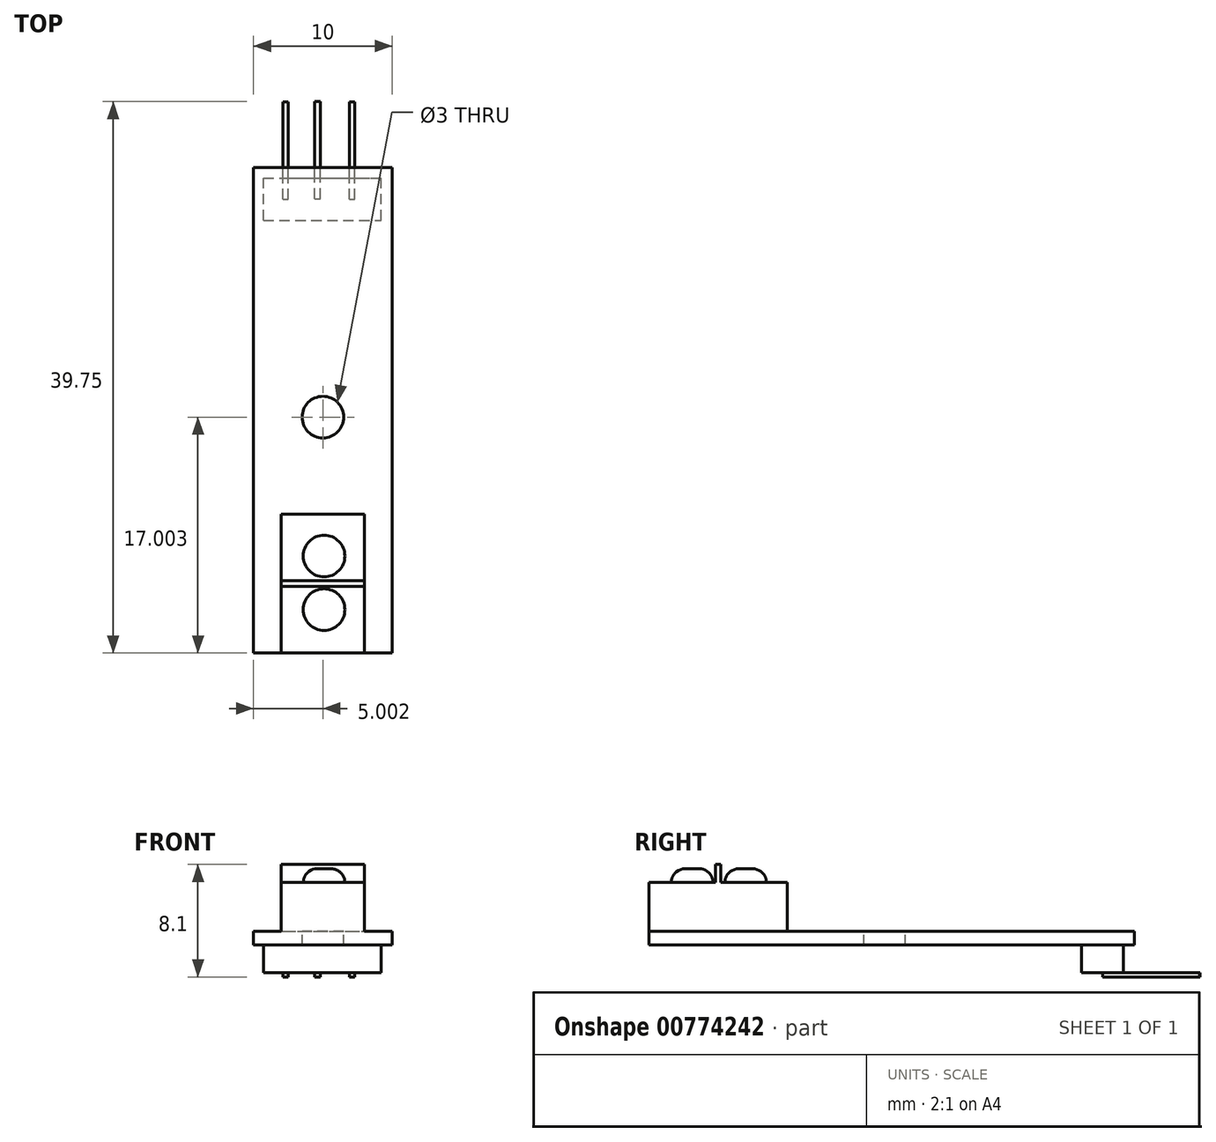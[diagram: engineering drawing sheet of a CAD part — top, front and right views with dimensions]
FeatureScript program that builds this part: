
annotation { "Feature Type Name" : "Feature", "Feature Type Description" : "" }
export const myFeature = defineFeature(function(context is Context, id is Id, definition is map)
    precondition{}
    {
        {
            var Q0;
            Q0=qCreatedBy(makeId("Top.planeOp"),FACE);
            var sketch = newSketch(context, id + "F0", { "sketchPlane" : qUnion([Q0])});
            skLineSegment(sketch, "E0.bottom", {"start": v(-16.49, 28.01) * mm, "end": v(-6.49, 28.01) * mm});
            skLineSegment(sketch, "E0.top", {"start": v(-16.49, -6.99) * mm, "end": v(-6.49, -6.99) * mm});
            skLineSegment(sketch, "E0.left", {"start": v(-16.49, 28.01) * mm, "end": v(-16.49, -6.99) * mm});
            skLineSegment(sketch, "E0.right", {"start": v(-6.49, 28.01) * mm, "end": v(-6.49, -6.99) * mm});
            skSolve(sketch);
        }
        {
            var Q0;
            Q0 = qSketchRegion(id + "F0", true);
            extrude(context, id + "F1", {"entities" : qUnion([Q0]), "depth" : 1 * mm, "offsetDistance" : 25 * mm});
        }
        {
            var Q0;
            Q0=makeQuery(id+"F1.opExtrude","CAP_FACE",FACE,{"disambiguationData":[OSD([sQuery(id+"F0.wireOp",EDGE,"E0.bottom"),sQuery(id+"F0.wireOp",EDGE,"E0.top"),sQuery(id+"F0.wireOp",EDGE,"E0.left"),sQuery(id+"F0.wireOp",EDGE,"E0.right")])],"isStart":false});
            var sketch = newSketch(context, id + "F2", { "sketchPlane" : qUnion([Q0])});
            skLineSegment(sketch, "E1.bottom", {"start": v(-14.49, -6.99) * mm, "end": v(-8.49, -6.99) * mm});
            skLineSegment(sketch, "E1.top", {"start": v(-14.49, 3.01) * mm, "end": v(-8.49, 3.01) * mm});
            skLineSegment(sketch, "E1.left", {"start": v(-14.49, -6.99) * mm, "end": v(-14.49, 3.01) * mm});
            skLineSegment(sketch, "E1.right", {"start": v(-8.49, -6.99) * mm, "end": v(-8.49, 3.01) * mm});
            skSolve(sketch);
        }
        {
            var Q0;
            Q0 = qSketchRegion(id + "F2", true);
            extrude(context, id + "F3", {"entities" : qUnion([Q0]), "operationType" : NewBodyOperationType.ADD, "depth" : 3.5 * mm, "offsetDistance" : 25 * mm});
        }
        {
            var Q0;
            Q0=makeQuery(id+"F3.opExtrude","CAP_FACE",FACE,{"disambiguationData":[OSD([sQuery(id+"F2.wireOp",EDGE,"E1.bottom"),sQuery(id+"F2.wireOp",EDGE,"E1.top"),sQuery(id+"F2.wireOp",EDGE,"E1.left"),sQuery(id+"F2.wireOp",EDGE,"E1.right")])],"isStart":false});
            var sketch = newSketch(context, id + "F4", { "sketchPlane" : qUnion([Q0])});
            skLineSegment(sketch, "E2", {"start": v(-14.49, -1.99) * mm, "end": v(-8.49, -1.99) * mm});
            skCircle(sketch, "E3", {"center": v(-11.4, -3.86) * mm, "radius": 1.5 * mm});
            skCircle(sketch, "E4", {"center": v(-11.4, 0) * mm, "radius": 1.5 * mm});
            skSolve(sketch);
        }
        {
            var Q0;
            Q0=makeQuery(id+"F4.imprint","IMPRINT",FACE,{"disambiguationData":[TD([[makeQuery(id+"F4.imprint","IMPRINT",EDGE,{"derivedFrom":sQuery(id+"F4.wireOp",EDGE,"E4")}),1.0]])]});
            var Q1;
            Q1=makeQuery(id+"F4.imprint","IMPRINT",FACE,{"disambiguationData":[TD([[makeQuery(id+"F4.imprint","IMPRINT",EDGE,{"derivedFrom":sQuery(id+"F4.wireOp",EDGE,"E3")}),1.0]])]});
            extrude(context, id + "F5", {"entities" : qUnion([Q0, Q1]), "operationType" : NewBodyOperationType.ADD, "depth" : 1 * mm, "offsetDistance" : 25 * mm});
        }
        {
            var Q0;
            Q0=makeQuery(id+"F1.opExtrude","CAP_FACE",FACE,{"disambiguationData":[OSD([sQuery(id+"F0.wireOp",EDGE,"E0.bottom"),sQuery(id+"F0.wireOp",EDGE,"E0.top"),sQuery(id+"F0.wireOp",EDGE,"E0.left"),sQuery(id+"F0.wireOp",EDGE,"E0.right")])],"isStart":true});
            var sketch = newSketch(context, id + "F6", { "sketchPlane" : qUnion([Q0])});
            skLineSegment(sketch, "E5.bottom", {"start": v(-15.78, -24.2) * mm, "end": v(-7.3, -24.2) * mm});
            skLineSegment(sketch, "E5.top", {"start": v(-15.78, -27.23) * mm, "end": v(-7.3, -27.23) * mm});
            skLineSegment(sketch, "E5.left", {"start": v(-15.78, -24.2) * mm, "end": v(-15.78, -27.23) * mm});
            skLineSegment(sketch, "E5.right", {"start": v(-7.3, -24.2) * mm, "end": v(-7.3, -27.23) * mm});
            skSolve(sketch);
        }
        {
            var Q0;
            Q0 = qSketchRegion(id + "F6", true);
            extrude(context, id + "F7", {"entities" : qUnion([Q0]), "operationType" : NewBodyOperationType.ADD, "depth" : 2 * mm, "offsetDistance" : 25 * mm});
        }
        {
            var Q0;
            Q0=makeQuery(id+"F7.opExtrude","CAP_FACE",FACE,{"disambiguationData":[OSD([sQuery(id+"F6.wireOp",EDGE,"E5.bottom"),sQuery(id+"F6.wireOp",EDGE,"E5.top"),sQuery(id+"F6.wireOp",EDGE,"E5.left"),sQuery(id+"F6.wireOp",EDGE,"E5.right")])],"isStart":false});
            var sketch = newSketch(context, id + "F8", { "sketchPlane" : qUnion([Q0])});
            skPoint(sketch, "E6.startSnap0", {"position": v(-15.78, -25.72) * mm});
            skLineSegment(sketch, "E7.bottom", {"start": v(-14.38, -25.72) * mm, "end": v(-13.99, -25.72) * mm});
            skLineSegment(sketch, "E7.top", {"start": v(-14.38, -32.72) * mm, "end": v(-13.99, -32.72) * mm});
            skLineSegment(sketch, "E7.left", {"start": v(-14.38, -25.72) * mm, "end": v(-14.38, -32.72) * mm});
            skLineSegment(sketch, "E7.right", {"start": v(-13.99, -25.72) * mm, "end": v(-13.99, -32.72) * mm});
            skPoint(sketch, "E8.startSnap0", {"position": v(-12.73, -25.76) * mm});
            skLineSegment(sketch, "E9.bottom", {"start": v(-12.07, -25.76) * mm, "end": v(-11.68, -25.76) * mm});
            skLineSegment(sketch, "E9.top", {"start": v(-12.07, -32.76) * mm, "end": v(-11.68, -32.76) * mm});
            skLineSegment(sketch, "E9.left", {"start": v(-12.07, -25.76) * mm, "end": v(-12.07, -32.76) * mm});
            skLineSegment(sketch, "E9.right", {"start": v(-11.68, -25.76) * mm, "end": v(-11.68, -32.76) * mm});
            skPoint(sketch, "E10.startSnap0", {"position": v(-10.98, -25.72) * mm});
            skLineSegment(sketch, "E11.bottom", {"start": v(-9.58, -25.72) * mm, "end": v(-9.19, -25.72) * mm});
            skLineSegment(sketch, "E11.top", {"start": v(-9.58, -32.72) * mm, "end": v(-9.19, -32.72) * mm});
            skLineSegment(sketch, "E11.left", {"start": v(-9.58, -25.72) * mm, "end": v(-9.58, -32.72) * mm});
            skLineSegment(sketch, "E11.right", {"start": v(-9.19, -25.72) * mm, "end": v(-9.19, -32.72) * mm});
            skSolve(sketch);
        }
        {
            var Q0;
            Q0 = qSketchRegion(id + "F8", true);
            extrude(context, id + "F9", {"entities" : qUnion([Q0]), "operationType" : NewBodyOperationType.ADD, "depth" : 0.3 * mm, "offsetDistance" : 25 * mm});
        }
        {
            var Q0;
            Q0=makeQuery(id+"F1.opExtrude","CAP_FACE",FACE,{"disambiguationData":[OSD([sQuery(id+"F0.wireOp",EDGE,"E0.bottom"),sQuery(id+"F0.wireOp",EDGE,"E0.top"),sQuery(id+"F0.wireOp",EDGE,"E0.left"),sQuery(id+"F0.wireOp",EDGE,"E0.right")])],"isStart":false});
            var sketch = newSketch(context, id + "F10", { "sketchPlane" : qUnion([Q0])});
            skCircle(sketch, "E12", {"center": v(-11.49, 10.01) * mm, "radius": 1.5 * mm});
            skSolve(sketch);
        }
        {
            var Q0;
            Q0=makeQuery(id+"F10.imprint","IMPRINT",FACE,{"disambiguationData":[TD([[makeQuery(id+"F10.imprint","IMPRINT",EDGE,{"derivedFrom":sQuery(id+"F10.wireOp",EDGE,"E12")}),1.0]])]});
            extrude(context, id + "F11", {"entities" : qUnion([Q0]), "operationType" : NewBodyOperationType.REMOVE, "endBound" : BoundingType.THROUGH_ALL, "oppositeDirection" : true, "depth" : 25 * mm, "offsetDistance" : 25 * mm});
        }
        {
            var Q0;
            Q0=makeQuery(id+"F5.opExtrude","CAP_EDGE",EDGE,{"disambiguationData":[OSD([sQuery(id+"F4.wireOp",EDGE,"E3")])],"isStart":false});
            var Q1;
            Q1=makeQuery(id+"F5.opExtrude","CAP_EDGE",EDGE,{"disambiguationData":[OSD([sQuery(id+"F4.wireOp",EDGE,"E4")])],"isStart":false});
            fillet(context, id + "F12", {"entities" : qUnion([Q0, Q1]), "radius" : 1 * mm, "tangentPropagation" : true, "allowEdgeOverflow" : false});
        }
        {
            var Q0;
            Q0=makeQuery(id+"F3.opExtrude","CAP_FACE",FACE,{"disambiguationData":[OSD([sQuery(id+"F2.wireOp",EDGE,"E1.bottom"),sQuery(id+"F2.wireOp",EDGE,"E1.top"),sQuery(id+"F2.wireOp",EDGE,"E1.left"),sQuery(id+"F2.wireOp",EDGE,"E1.right")])],"isStart":false});
            var sketch = newSketch(context, id + "F13", { "sketchPlane" : qUnion([Q0])});
            skLineSegment(sketch, "E13", {"start": v(-14.49, -1.99) * mm, "end": v(-8.49, -1.99) * mm, "construction": true});
            skLineSegment(sketch, "E14.0", {"start": v(-14.49, -2.19) * mm, "end": v(-8.49, -2.19) * mm});
            skLineSegment(sketch, "E15.0", {"start": v(-14.49, -1.79) * mm, "end": v(-8.49, -1.79) * mm});
            skSolve(sketch);
        }
        {
            var Q0;
            {var subQ0=sQuery(id+"F13.wireOp",EDGE,"E14.0");Q0=makeQuery(id+"F13.imprint","IMPRINT",FACE,{"disambiguationData":[TD([[makeQuery(id+"F13.imprint","IMPRINT",EDGE,{"derivedFrom":subQ0}),1.0]])]});}
            extrude(context, id + "F14", {"entities" : qUnion([Q0]), "operationType" : NewBodyOperationType.ADD, "depth" : 1.3 * mm, "offsetDistance" : 25 * mm});
        }
    });
